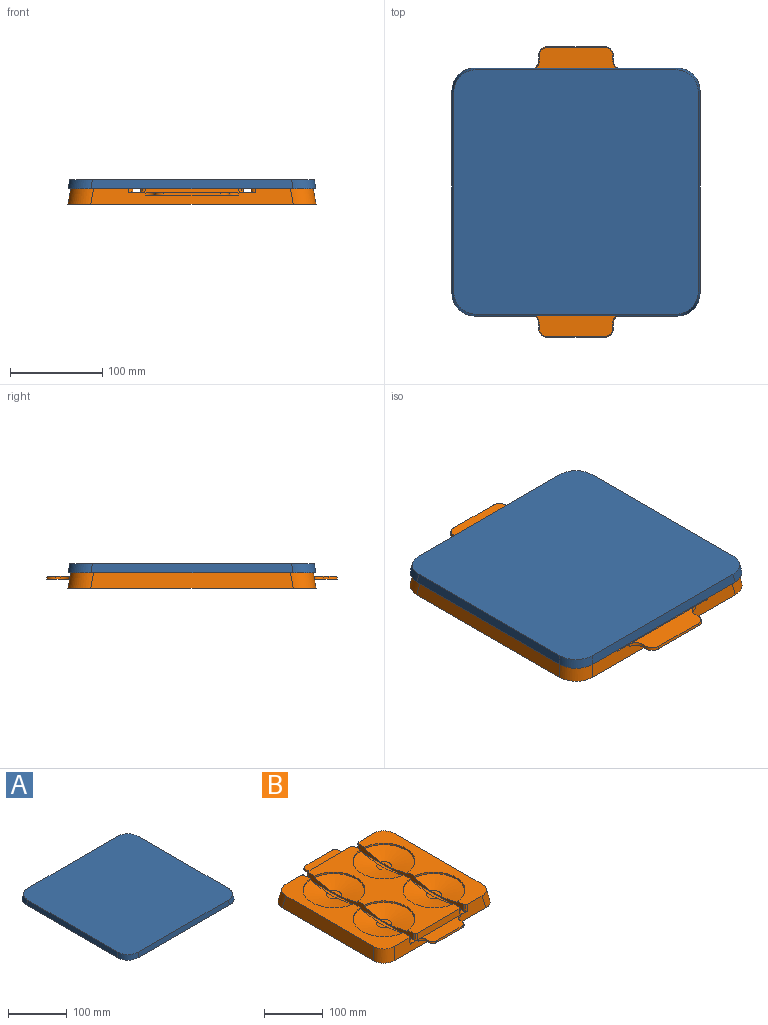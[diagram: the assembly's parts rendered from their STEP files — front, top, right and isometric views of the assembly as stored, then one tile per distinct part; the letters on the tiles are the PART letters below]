
ASSEMBLY  parts=2 mates=1
PART A: 19 faces, bbox 269.1x269.1x13.4 mm
  f0: plane 268.53x268.53mm, normal (0,0,-1), area 2085.7mm2, adj f1,f2,f3,f4,f6,f7,f8,f9
  f1: plane 219.29x10mm, normal (0,0.98,0.17), area 2208.8mm2, adj f0,f5,f6,f9
  f2: plane 219.29x10mm, normal (-0.98,0,0.17), area 2208.8mm2, adj f0,f5,f6,f7
  f3: plane 219.29x10mm, normal (0,-0.98,0.17), area 2208.8mm2, adj f0,f5,f7,f8
  f4: plane 219.29x10mm, normal (0.98,0,0.17), area 2208.8mm2, adj f0,f5,f8,f9
  f5: plane 265x265mm, normal (0,0,1), area 69709.8mm2, adj f1,f2,f3,f4,f6,f7,f8,f9
  f6: cylinder r=25mm len=26.69mm, axis (-0.17,0.17,-0.97), area 397mm2, adj f0,f1,f2,f5
  f7: cylinder r=25mm len=26.69mm, axis (-0.17,-0.17,-0.97), area 397mm2, adj f0,f2,f3,f5
  f8: cylinder r=25mm len=26.69mm, axis (0.17,-0.17,-0.97), area 397mm2, adj f0,f3,f4,f5
  f9: cylinder r=25mm len=26.69mm, axis (0.17,0.17,-0.97), area 397mm2, adj f0,f1,f4,f5
  f10: plane 219.16x8mm, normal (0,-0.98,-0.17), area 1768.9mm2, adj f0,f14,f15,f18
  f11: plane 219.16x8mm, normal (0.98,0,-0.17), area 1768.9mm2, adj f0,f14,f15,f16
  f12: plane 219.16x8mm, normal (0,0.98,-0.17), area 1768.9mm2, adj f0,f14,f16,f17
  f13: plane 219.16x8mm, normal (-0.98,0,-0.17), area 1768.9mm2, adj f0,f14,f17,f18
  f14: plane 261.64x261.64mm, normal (0,0,-1), area 68021.3mm2, adj f10,f11,f12,f13,f15,f16,f17,f18
  f15: cylinder r=23mm len=24.34mm, axis (-0.17,0.17,-0.97), area 292.2mm2, adj f0,f10,f11,f14
  f16: cylinder r=23mm len=24.34mm, axis (-0.17,-0.17,-0.97), area 292.2mm2, adj f0,f11,f12,f14
  f17: cylinder r=23mm len=24.34mm, axis (0.17,-0.17,-0.97), area 292.2mm2, adj f0,f12,f13,f14
  f18: cylinder r=23mm len=24.34mm, axis (0.17,0.17,-0.97), area 292.2mm2, adj f0,f10,f13,f14
PART B: 109 faces, bbox 270x316.1x29 mm
  f0: plane 219.58x25mm, normal (0,0.98,0.17), area 4697.8mm2, adj f2,f3,f4,f19,f32,f35,f36,f39
  f1: plane 219.58x25mm, normal (0,-0.98,0.17), area 4697.8mm2, adj f2,f3,f4,f19,f33,f34,f36,f39
  f2: plane 268.82x268.82mm, normal (0,0,-1), area 2088.1mm2, adj f0,f1,f17,f18,f32,f33,f34,f35
  f3: plane 260.54x65.54mm, normal (0,0,1), area 9021.2mm2, adj f0,f1,f5,f9,f17,f32,f33,f37
  f4: plane 260.54x110.54mm, normal (0,0,1), area 13357.7mm2, adj f0,f1,f7,f11,f20,f24,f38,f41
  f5: cone r=52.5mm half-angle=5deg, axis (0,0,1), area 465mm2, adj f3,f16,f37
  f6: plane 23.6x8.38mm, normal (0,0,1), area 144.2mm2, adj f16,f37
  f7: cone r=52.5mm half-angle=5deg, axis (0,0,1), area 465mm2, adj f4,f13,f41
  f8: plane 23.6x8.38mm, normal (0,0,1), area 144.2mm2, adj f13,f41
  f9: cone r=52.5mm half-angle=5deg, axis (0,0,1), area 465mm2, adj f3,f14,f37
  f10: plane 23.6x8.38mm, normal (0,0,1), area 144.2mm2, adj f14,f37
  f11: cone r=52.5mm half-angle=5deg, axis (0,0,1), area 465mm2, adj f4,f15,f41
  f12: plane 23.6x8.38mm, normal (0,0,1), area 144.2mm2, adj f15,f41
  f13: cone r=12.5mm half-angle=80deg, axis (0,0,1), area 3744mm2, adj f7,f8,f41
  f14: cone r=12.5mm half-angle=80deg, axis (0,0,1), area 3744mm2, adj f9,f10,f37
  f15: cone r=12.5mm half-angle=80deg, axis (0,0,1), area 3744mm2, adj f11,f12,f41
  f16: cone r=12.5mm half-angle=80deg, axis (0,0,1), area 3744mm2, adj f5,f6,f37
  f17: plane 219.58x25mm, normal (-0.98,0,0.17), area 5462.2mm2, adj f2,f3,f32,f33
  f18: plane 219.58x25mm, normal (0.98,0,0.17), area 5462.2mm2, adj f2,f19,f34,f35
  f19: plane 260.54x65.54mm, normal (0,0,1), area 9021.2mm2, adj f0,f1,f18,f22,f26,f34,f35,f40
  f20: cone r=52.5mm half-angle=5deg, axis (0,0,1), area 465mm2, adj f4,f31,f38
  f21: plane 23.6x8.38mm, normal (0,0,1), area 144.2mm2, adj f31,f38
  f22: cone r=52.5mm half-angle=5deg, axis (0,0,1), area 465mm2, adj f19,f28,f40
  f23: plane 23.6x8.38mm, normal (0,0,1), area 144.2mm2, adj f28,f40
  f24: cone r=52.5mm half-angle=5deg, axis (0,0,1), area 465mm2, adj f4,f29,f38
  f25: plane 23.6x8.38mm, normal (0,0,1), area 144.2mm2, adj f29,f38
  f26: cone r=52.5mm half-angle=5deg, axis (0,0,1), area 465mm2, adj f19,f30,f40
  f27: plane 23.6x8.38mm, normal (0,0,1), area 144.2mm2, adj f30,f40
  f28: cone r=12.5mm half-angle=80deg, axis (0,0,1), area 3744mm2, adj f22,f23,f40
  f29: cone r=12.5mm half-angle=80deg, axis (0,0,1), area 3744mm2, adj f24,f25,f38
  f30: cone r=12.5mm half-angle=80deg, axis (0,0,1), area 3744mm2, adj f26,f27,f40
  f31: cone r=12.5mm half-angle=80deg, axis (0,0,1), area 3744mm2, adj f20,f21,f38
  f32: cylinder r=25mm len=29.33mm, axis (-0.17,0.17,-0.97), area 992.4mm2, adj f0,f2,f3,f17
  f33: cylinder r=25mm len=29.33mm, axis (-0.17,-0.17,-0.97), area 992.4mm2, adj f1,f2,f3,f17
  f34: cylinder r=25mm len=29.33mm, axis (0.17,-0.17,-0.97), area 992.4mm2, adj f1,f2,f18,f19
  f35: cylinder r=25mm len=29.33mm, axis (0.17,0.17,-0.97), area 992.4mm2, adj f0,f2,f18,f19
  f36: plane 264.77x18.32mm, normal (0,0,1), area 2108.6mm2, adj f0,f1,f37,f38,f87,f88,f89,f90
  f37: plane 254.23x12mm, normal (1,0,0.09), area 1509.3mm2, adj f3,f5,f6,f9,f10,f14,f16,f36
  f38: plane 254.23x12mm, normal (-1,0,0.09), area 1509.3mm2, adj f4,f20,f21,f24,f25,f29,f31,f36
  f39: plane 264.77x18.32mm, normal (0,0,1), area 2108.6mm2, adj f0,f1,f40,f41,f83,f84,f85,f86
  f40: plane 254.23x12mm, normal (-1,0,0.09), area 1509.3mm2, adj f19,f22,f23,f26,f27,f28,f30,f39
  f41: plane 254.23x12mm, normal (1,0,0.09), area 1509.3mm2, adj f4,f7,f8,f11,f12,f13,f15,f39
  f42: plane 219.45x23mm, normal (0,-0.98,-0.17), area 4723.1mm2, adj f2,f44,f45,f60,f73,f76,f77,f78
  f43: plane 219.45x23mm, normal (0,0.98,-0.17), area 4723.1mm2, adj f2,f44,f45,f60,f74,f75,f77,f78
  f44: plane 256.64x61.49mm, normal (0,0,-1), area 7769.7mm2, adj f42,f43,f46,f50,f58,f73,f74,f78
  f45: plane 256.64x106.33mm, normal (0,0,-1), area 11704mm2, adj f42,f43,f48,f52,f61,f65,f79,f82
  f46: cone r=54.49mm half-angle=5deg, axis (0,0,1), area 424.5mm2, adj f44,f57,f78
  f47: plane 22.38x6.72mm, normal (0,0,-1), area 107.1mm2, adj f57,f78
  f48: cone r=54.49mm half-angle=5deg, axis (0,0,1), area 424.5mm2, adj f45,f54,f82
  f49: plane 22.38x6.72mm, normal (0,0,-1), area 107.1mm2, adj f54,f82
  f50: cone r=54.49mm half-angle=5deg, axis (0,0,1), area 424.5mm2, adj f44,f55,f78
  f51: plane 22.38x6.72mm, normal (0,0,-1), area 107.1mm2, adj f55,f78
  f52: cone r=54.49mm half-angle=5deg, axis (0,0,1), area 424.5mm2, adj f45,f56,f82
  f53: plane 22.38x6.72mm, normal (0,0,-1), area 107.1mm2, adj f56,f82
  f54: cone r=12.85mm half-angle=80deg, axis (0,0,1), area 3878.5mm2, adj f48,f49,f82
  f55: cone r=12.85mm half-angle=80deg, axis (0,0,1), area 3878.5mm2, adj f50,f51,f78
  f56: cone r=12.85mm half-angle=80deg, axis (0,0,1), area 3878.5mm2, adj f52,f53,f82
  f57: cone r=12.85mm half-angle=80deg, axis (0,0,1), area 3878.5mm2, adj f46,f47,f78
  f58: plane 219.45x23mm, normal (0.98,0,-0.17), area 5030.6mm2, adj f2,f44,f73,f74
  f59: plane 219.45x23mm, normal (-0.98,0,-0.17), area 5030.6mm2, adj f2,f60,f75,f76
  f60: plane 256.64x61.49mm, normal (0,0,-1), area 7769.7mm2, adj f42,f43,f59,f63,f67,f75,f76,f81
  f61: cone r=54.49mm half-angle=5deg, axis (0,0,1), area 424.5mm2, adj f45,f72,f79
  f62: plane 22.38x6.72mm, normal (0,0,-1), area 107.1mm2, adj f72,f79
  f63: cone r=54.49mm half-angle=5deg, axis (0,0,1), area 424.5mm2, adj f60,f69,f81
  f64: plane 22.38x6.72mm, normal (0,0,-1), area 107.1mm2, adj f69,f81
  f65: cone r=54.49mm half-angle=5deg, axis (0,0,1), area 424.5mm2, adj f45,f70,f79
  f66: plane 22.38x6.72mm, normal (0,0,-1), area 107.1mm2, adj f70,f79
  f67: cone r=54.49mm half-angle=5deg, axis (0,0,1), area 424.5mm2, adj f60,f71,f81
  f68: plane 22.38x6.72mm, normal (0,0,-1), area 107.1mm2, adj f71,f81
  f69: cone r=12.85mm half-angle=80deg, axis (0,0,1), area 3878.5mm2, adj f63,f64,f81
  f70: cone r=12.85mm half-angle=80deg, axis (0,0,1), area 3878.5mm2, adj f65,f66,f79
  f71: cone r=12.85mm half-angle=80deg, axis (0,0,1), area 3878.5mm2, adj f67,f68,f81
  f72: cone r=12.85mm half-angle=80deg, axis (0,0,1), area 3878.5mm2, adj f61,f62,f79
  f73: cylinder r=23mm len=26.98mm, axis (-0.17,0.17,-0.97), area 840mm2, adj f2,f42,f44,f58
  f74: cylinder r=23mm len=26.98mm, axis (-0.17,-0.17,-0.97), area 840mm2, adj f2,f43,f44,f58
  f75: cylinder r=23mm len=26.98mm, axis (0.17,-0.17,-0.97), area 840mm2, adj f2,f43,f59,f60
  f76: cylinder r=23mm len=26.98mm, axis (0.17,0.17,-0.97), area 840mm2, adj f2,f42,f59,f60
  f77: plane 260.88x11.57mm, normal (0,0,-1), area 3017.2mm2, adj f42,f43,f78,f79
  f78: plane 260.88x12mm, normal (-1,0,-0.09), area 1575.6mm2, adj f42,f43,f44,f46,f47,f50,f51,f55
  f79: plane 260.88x12mm, normal (1,0,-0.09), area 1575.6mm2, adj f42,f43,f45,f61,f62,f65,f66,f70
  f80: plane 260.88x11.57mm, normal (0,0,-1), area 3017.2mm2, adj f42,f43,f81,f82
  f81: plane 260.88x12mm, normal (1,0,-0.09), area 1575.6mm2, adj f42,f43,f60,f63,f64,f67,f68,f69
  f82: plane 260.88x12mm, normal (-1,0,-0.09), area 1575.6mm2, adj f42,f43,f45,f48,f49,f52,f53,f54
  f83: cylinder r=5mm len=12.96mm, axis (-0.09,0.17,-0.98), area 95.1mm2, adj f0,f19,f39,f40
  f84: cylinder r=5mm len=12.96mm, axis (-0.09,-0.17,-0.98), area 95.1mm2, adj f1,f19,f39,f40
  f85: cylinder r=5mm len=12.96mm, axis (0.09,0.17,-0.98), area 95.1mm2, adj f0,f4,f39,f41
  f86: cylinder r=5mm len=12.96mm, axis (0.09,-0.17,-0.98), area 95.1mm2, adj f1,f4,f39,f41
  f87: cylinder r=5mm len=12.96mm, axis (0.09,0.17,-0.98), area 95.1mm2, adj f0,f3,f36,f37
  f88: cylinder r=5mm len=12.96mm, axis (0.09,-0.17,-0.98), area 95.1mm2, adj f1,f3,f36,f37
  f89: cylinder r=5mm len=12.96mm, axis (-0.09,0.17,-0.98), area 95.1mm2, adj f0,f4,f36,f38
  f90: cylinder r=5mm len=12.96mm, axis (-0.09,-0.17,-0.98), area 95.1mm2, adj f1,f4,f36,f38
  f91: plane 5.83x3mm, normal (-0.98,0,0.17), area 16.2mm2, adj f93,f95,f103,f107
  f92: plane 5.83x3mm, normal (0.98,0,0.17), area 16.2mm2, adj f93,f95,f104,f108
  f93: plane 100.75x25mm, normal (0,0,-1), area 2026.4mm2, adj f1,f91,f92,f94,f103,f104,f107,f108
  f94: plane 61.36x3mm, normal (0,-0.98,0.17), area 185.3mm2, adj f93,f95,f107,f108
  f95: plane 99.7x25mm, normal (0,0,1), area 2000mm2, adj f1,f91,f92,f94,f103,f104,f107,f108
  f96: plane 61.36x3mm, normal (0,0.98,0.17), area 185.3mm2, adj f99,f100,f105,f106
  f97: plane 5.83x3mm, normal (-0.98,0,0.17), area 16.2mm2, adj f99,f100,f101,f105
  f98: plane 5.83x3mm, normal (0.98,0,0.17), area 16.2mm2, adj f99,f100,f102,f106
  f99: plane 100.75x25mm, normal (0,0,-1), area 2026.4mm2, adj f0,f96,f97,f98,f101,f102,f105,f106
  f100: plane 99.7x25mm, normal (0,0,1), area 2000mm2, adj f0,f96,f97,f98,f101,f102,f105,f106
  f101: cylinder r=10mm len=10.5mm, axis (0.17,-0.17,0.97), area 47.6mm2, adj f0,f97,f99,f100
  f102: cylinder r=10mm len=10.5mm, axis (-0.17,-0.17,0.97), area 47.6mm2, adj f0,f98,f99,f100
  f103: cylinder r=10mm len=10.5mm, axis (-0.17,-0.17,-0.97), area 47.6mm2, adj f1,f91,f93,f95
  f104: cylinder r=10mm len=10.5mm, axis (0.17,-0.17,-0.97), area 47.6mm2, adj f1,f92,f93,f95
  f105: cylinder r=10mm len=10.5mm, axis (0.17,-0.17,0.97), area 47.6mm2, adj f96,f97,f99,f100
  f106: cylinder r=10mm len=10.5mm, axis (-0.17,-0.17,0.97), area 47.6mm2, adj f96,f98,f99,f100
  f107: cylinder r=10mm len=10.5mm, axis (0.17,0.17,0.97), area 47.6mm2, adj f91,f93,f94,f95
  f108: cylinder r=10mm len=10.5mm, axis (-0.17,0.17,0.97), area 47.6mm2, adj f92,f93,f94,f95
PLACE A t=(-86.71,-93.46,-76.01)mm
PLACE B t=(-84.21,-95.96,-93.01)mm
MATE fastened B.f4 <-> A.f14  axis (0,0,1) through (-84.21,-95.96,-68.01)mm
